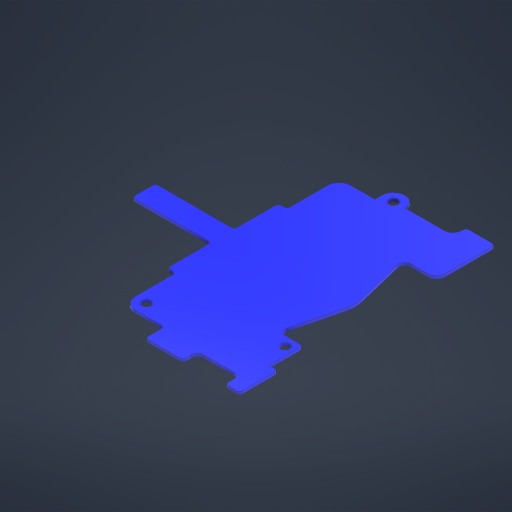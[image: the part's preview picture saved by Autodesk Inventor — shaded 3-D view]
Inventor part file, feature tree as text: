
AUTODESK INVENTOR PART (.ipt)
format: ipt  version: 2024 (Build 280153000, 153)  size: 382,464 bytes
history: native  units: in
note: dims shown in document units (in); Inventor stores cm internally (conversion verified against a paired STEP export)
features: plane x1, extrude x1, sketch x1
ambient origin geometry x8: Origin, YZ Plane, XZ Plane, XY Plane, X Axis, Y Axis, Z Axis, Center Point
bodies: Body1 (feature_tree)
feature tree (3):
  plane  "Work Plane2"
  extrude  "Extrusion2"  Depth=0.0394in TaperAngle=0.0deg
  sketch  "Sketch2"  dims[d13=0.122in d15=0.122in d16=0.0394in d17=0.0in d26=0.0394in d27=0.1181in d32=0.0394in d33=0.7957in d36=0.5512in d37=0.1181in d38=0.5512in d39=0.1181in d40=0.0394in d42=0.5118in d43=0.0394in d47=3.4646in d49=0.1575in d50=0.0787in d51=0.0787in d52=0.0197in d57=0.0394in d58=1.6929in d60=0.8465in d61=0.0787in d62=0.3937in]
